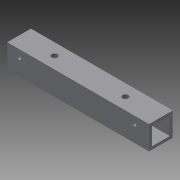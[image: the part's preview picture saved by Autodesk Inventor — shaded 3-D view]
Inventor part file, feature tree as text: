
AUTODESK INVENTOR PART (.ipt)
format: ipt  version: 2015 SP1 (Build 190203100, 203)  size: 103,936 bytes
history: native  units: in
note: dims shown in document units (in); Inventor stores cm internally (conversion verified against a paired STEP export)
features: sketch x3, hole x2, extrude x1
ambient origin geometry x8: Origin, YZ Plane, XZ Plane, XY Plane, X Axis, Y Axis, Z Axis, Center Point
bodies: Solid1 (feature_tree)
feature tree (6):
  extrude  "Extrusion1"  Depth=1.0in
  hole  "Hole1"  [1 undecoded]
  hole  "Hole2"  [1 undecoded]
  sketch  "Sketch1"  dims[d0=1.0in d1=1.0in]
  sketch  "Sketch2"  dims[d2=0.75in d3=0.75in]
  sketch  "Sketch3"  dims[d4=0.125in d5=0.125in d6=6.0in d7=0.0in d8=1.5in d9=0.5in d10=0.5in d11=1.5in d12=0.25in d13=0.75in d14=0.375in d15=0.25in d16=0.5635in d17=1.0in d18=0.8108in d19=0.625in d20=0.6875in d21=0.5in d22=0.6875in d23=0.1719in d24=0.75in d25=0.375in d26=0.25in d27=0.5635in d28=1.0in d29=0.8108in]
note: 2 required parameter values undecoded (feature->parameter linkage not recoverable at this tier; creation-order binding heuristic only, values carry confidence <= 0.55)
